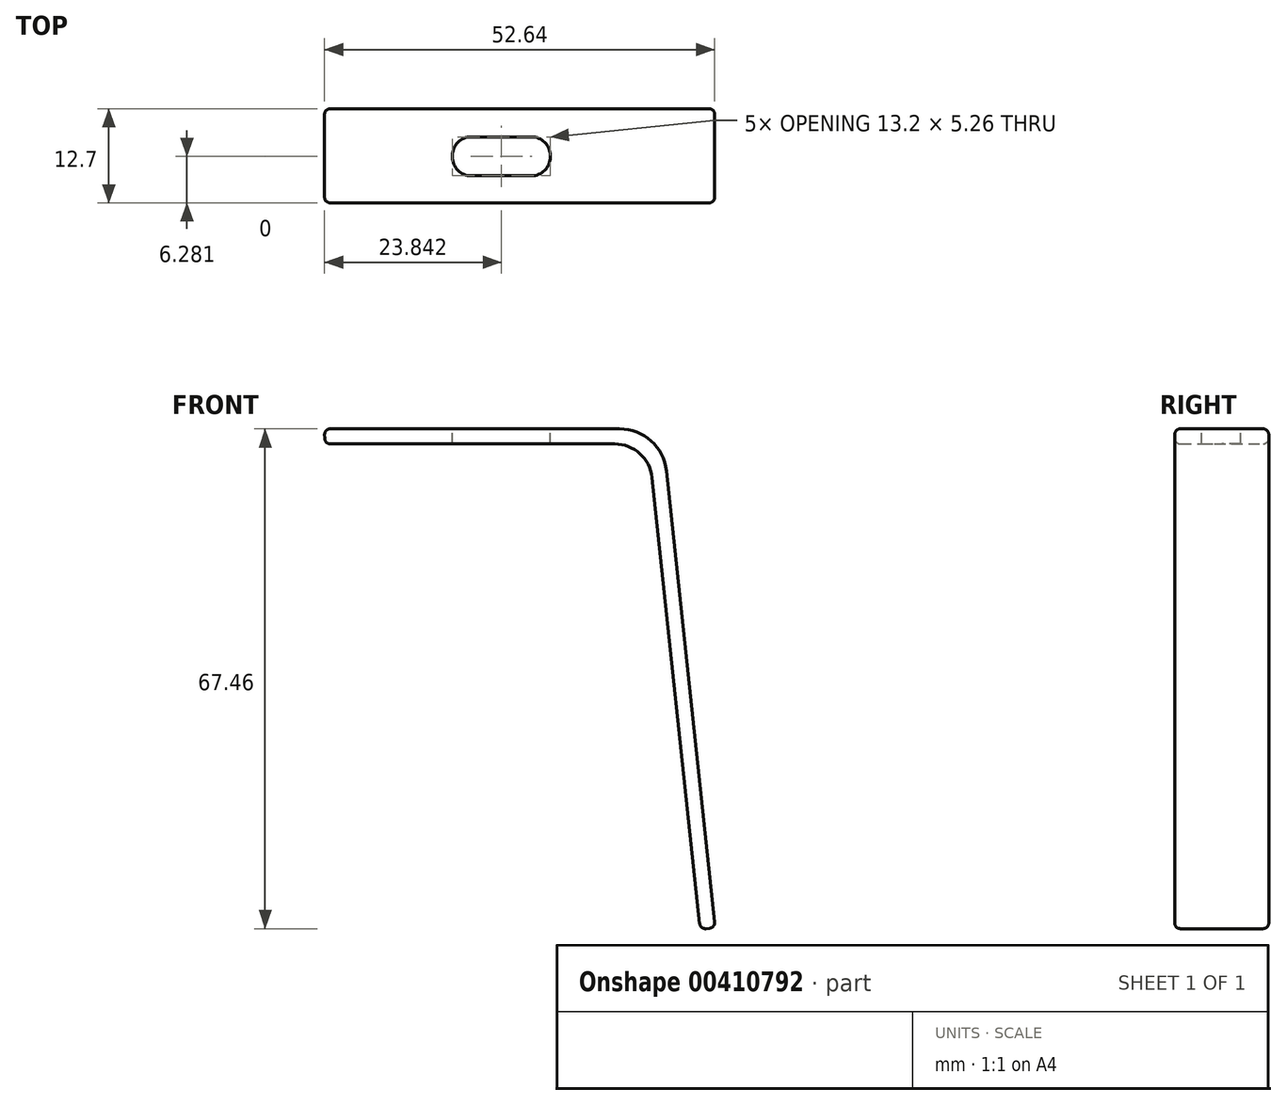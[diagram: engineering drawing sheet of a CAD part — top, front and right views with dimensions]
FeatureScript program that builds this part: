
annotation { "Feature Type Name" : "Feature", "Feature Type Description" : "" }
export const myFeature = defineFeature(function(context is Context, id is Id, definition is map)
    precondition{}
    {
        {
            var Q0;
            Q0=qCreatedBy(makeId("Front.planeOp"),FACE);
            var sketch = newSketch(context, id + "F0", { "sketchPlane" : qUnion([Q0])});
            skLineSegment(sketch, "E0", {"start": v(-69.9, 8.83) * mm, "end": v(-30.08, 8.83) * mm});
            skLineSegment(sketch, "E1", {"start": v(-23.77, 3.15) * mm, "end": v(-17.18, -58.49) * mm});
            skLineSegment(sketch, "E2", {"start": v(-17.18, -58.49) * mm, "end": v(-19.2, -58.7) * mm});
            skLineSegment(sketch, "E3", {"start": v(-19.2, -58.7) * mm, "end": v(-25.72, 2.26) * mm});
            skLineSegment(sketch, "E4", {"start": v(-30.77, 6.8) * mm, "end": v(-69.88, 6.8) * mm});
            skLineSegment(sketch, "E5", {"start": v(-69.88, 6.8) * mm, "end": v(-69.9, 8.83) * mm});
            skPoint(sketch, "E6.visualSharp", {"position": v(-24.38, 8.83) * mm});
            skArc(sketch, "E6.filletArc", {"start": v(-23.77, 3.15) * mm, "mid": v(-25.84, 7.2) * mm, "end": v(-30.08, 8.83) * mm});
            skPoint(sketch, "E7.visualSharp", {"position": v(-26.2, 6.8) * mm});
            skArc(sketch, "E7.filletArc", {"start": v(-25.72, 2.26) * mm, "mid": v(-27.37, 5.5) * mm, "end": v(-30.77, 6.8) * mm});
            skSolve(sketch);
        }
        {
            var Q0;
            Q0=makeQuery(id+"F0.imprint","IMPRINT",FACE,{"disambiguationData":[TD([[makeQuery(id+"F0.imprint","IMPRINT",EDGE,{"derivedFrom":sQuery(id+"F0.wireOp",EDGE,"E0")}),-1.0]])]});
            extrude(context, id + "F1", {"entities" : qUnion([Q0]), "depth" : 12.7 * mm});
        }
        {
            var Q0;
            Q0=makeQuery(id+"F1.opExtrude","SWEPT_FACE",FACE,{"disambiguationData":[OSD([sQuery(id+"F0.wireOp",EDGE,"E0")])]});
            var sketch = newSketch(context, id + "F2", { "sketchPlane" : qUnion([Q0])});
            skLineSegment(sketch, "E8.bottom", {"start": v(-50.12, -3.79) * mm, "end": v(-42, -3.79) * mm});
            skLineSegment(sketch, "E8.top", {"start": v(-50.12, -9.05) * mm, "end": v(-42, -9.05) * mm});
            skLineSegment(sketch, "E8.left", {"start": v(-52.66, -6.33) * mm, "end": v(-52.66, -6.51) * mm});
            skLineSegment(sketch, "E8.right", {"start": v(-39.46, -6.33) * mm, "end": v(-39.46, -6.51) * mm});
            skPoint(sketch, "E9.visualSharp", {"position": v(-52.66, -3.79) * mm});
            skArc(sketch, "E9.filletArc", {"start": v(-50.12, -3.79) * mm, "mid": v(-51.91, -4.53) * mm, "end": v(-52.66, -6.33) * mm});
            skPoint(sketch, "E10.visualSharp", {"position": v(-52.66, -9.05) * mm});
            skArc(sketch, "E10.filletArc", {"start": v(-52.66, -6.51) * mm, "mid": v(-51.91, -8.3) * mm, "end": v(-50.12, -9.05) * mm});
            skPoint(sketch, "E11.visualSharp", {"position": v(-39.46, -9.05) * mm});
            skArc(sketch, "E11.filletArc", {"start": v(-42, -9.05) * mm, "mid": v(-40.2, -8.3) * mm, "end": v(-39.46, -6.51) * mm});
            skPoint(sketch, "E12.visualSharp", {"position": v(-39.46, -3.79) * mm});
            skArc(sketch, "E12.filletArc", {"start": v(-39.46, -6.33) * mm, "mid": v(-40.2, -4.53) * mm, "end": v(-42, -3.79) * mm});
            skSolve(sketch);
        }
        {
            var Q0;
            Q0=makeQuery(id+"F2.imprint","IMPRINT",FACE,{"disambiguationData":[TD([[makeQuery(id+"F2.imprint","IMPRINT",EDGE,{"derivedFrom":sQuery(id+"F2.wireOp",EDGE,"E8.bottom")}),-1.0]])]});
            extrude(context, id + "F3", {"entities" : qUnion([Q0]), "operationType" : NewBodyOperationType.REMOVE, "oppositeDirection" : true, "depth" : 25.4 * mm});
        }
        {
            var Q0;
            Q0=makeQuery(id+"F1.opExtrude","CAP_EDGE",EDGE,{"disambiguationData":[OSD([sQuery(id+"F0.wireOp",EDGE,"E0")])],"isStart":false});
            var Q1;
            Q1=makeQuery(id+"F1.opExtrude","SWEPT_EDGE",EDGE,{"disambiguationData":[OSD([sQuery(id+"F0.wireOp",EDGE,"E1"),sQuery(id+"F0.wireOp",EDGE,"E2")])]});
            var Q2;
            Q2=makeQuery(id+"F1.opExtrude","CAP_EDGE",EDGE,{"disambiguationData":[OSD([sQuery(id+"F0.wireOp",EDGE,"E4")])],"isStart":false});
            var Q3;
            Q3=makeQuery(id+"F1.opExtrude","CAP_EDGE",EDGE,{"disambiguationData":[OSD([sQuery(id+"F0.wireOp",EDGE,"E1")])],"isStart":true});
            var Q4;
            Q4=makeQuery(id+"F1.opExtrude","CAP_EDGE",EDGE,{"disambiguationData":[OSD([sQuery(id+"F0.wireOp",EDGE,"E3")])],"isStart":true});
            var Q5;
            Q5=makeQuery(id+"F1.opExtrude","CAP_EDGE",EDGE,{"disambiguationData":[OSD([sQuery(id+"F0.wireOp",EDGE,"E2")])],"isStart":true});
            var Q6;
            Q6=makeQuery(id+"F1.opExtrude","SWEPT_EDGE",EDGE,{"disambiguationData":[OSD([sQuery(id+"F0.wireOp",EDGE,"E2"),sQuery(id+"F0.wireOp",EDGE,"E3")])]});
            var Q7;
            Q7=makeQuery(id+"F1.opExtrude","CAP_EDGE",EDGE,{"disambiguationData":[OSD([sQuery(id+"F0.wireOp",EDGE,"E2")])],"isStart":false});
            var Q8;
            Q8=makeQuery(id+"F1.opExtrude","SWEPT_EDGE",EDGE,{"disambiguationData":[OSD([sQuery(id+"F0.wireOp",EDGE,"E4"),sQuery(id+"F0.wireOp",EDGE,"E5")])]});
            var Q9;
            Q9=makeQuery(id+"F1.opExtrude","CAP_EDGE",EDGE,{"disambiguationData":[OSD([sQuery(id+"F0.wireOp",EDGE,"E5")])],"isStart":false});
            var Q10;
            Q10=makeQuery(id+"F1.opExtrude","SWEPT_EDGE",EDGE,{"disambiguationData":[OSD([sQuery(id+"F0.wireOp",EDGE,"E0"),sQuery(id+"F0.wireOp",EDGE,"E5")])]});
            var Q11;
            Q11=makeQuery(id+"F1.opExtrude","CAP_EDGE",EDGE,{"disambiguationData":[OSD([sQuery(id+"F0.wireOp",EDGE,"E5")])],"isStart":true});
            var Q12;
            Q12=makeQuery(id+"F1.opExtrude","CAP_EDGE",EDGE,{"disambiguationData":[OSD([sQuery(id+"F0.wireOp",EDGE,"E6.filletArc")])],"isStart":true});
            var Q13;
            Q13=makeQuery(id+"F1.opExtrude","CAP_EDGE",EDGE,{"disambiguationData":[OSD([sQuery(id+"F0.wireOp",EDGE,"E6.filletArc")])],"isStart":false});
            fillet(context, id + "F4", {"entities" : qUnion([Q0, Q1, Q2, Q3, Q4, Q5, Q6, Q7, Q8, Q9, Q10, Q11, Q12, Q13]), "radius" : 0.76 * mm, "tangentPropagation" : true, "allowEdgeOverflow" : false});
        }
    });
